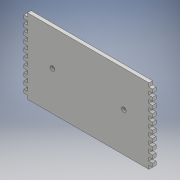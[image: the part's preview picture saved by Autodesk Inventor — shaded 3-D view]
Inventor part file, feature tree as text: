
AUTODESK INVENTOR PART (.ipt)
format: ipt  version: 2017 (Build 210142000, 142)  size: 253,952 bytes
history: native  units: mm
features: extrude x1, sketch x1
ambient origin geometry x8: Origin, YZ Plane, XZ Plane, XY Plane, X Axis, Y Axis, Z Axis, Center Point
bodies: Body1 (feature_tree)
feature tree (2):
  extrude  "Extrusion4"  Depth=6.35mm
  sketch  "Sketch5"  dims[d59=7.9375mm d73=6.35mm d79=6.35mm d80=6.35mm d81=6.35mm d82=6.35mm d92=6.35mm d93=6.35mm d94=6.35mm d95=6.35mm d96=6.35mm d97=6.35mm d100=6.35mm d101=6.35mm d102=6.35mm d103=6.35mm d106=6.35mm d107=6.35mm d108=6.35mm d109=6.35mm d112=6.35mm d113=6.35mm d114=6.35mm d115=6.35mm d118=6.35mm d119=6.35mm d120=6.35mm d121=6.35mm d124=6.35mm d125=6.35mm d126=6.35mm d127=6.35mm d130=6.35mm d131=6.35mm d132=6.35mm d133=6.35mm d136=6.35mm d137=6.35mm d138=6.35mm d139=6.35mm d143=6.35mm d149=6.35mm d150=6.35mm d151=6.35mm d152=6.35mm d153=6.35mm d154=6.35mm d155=6.35mm d156=6.35mm d157=6.35mm d158=6.35mm d159=6.35mm d160=6.35mm d161=6.35mm d162=6.35mm d163=6.35mm d164=6.35mm d165=6.35mm d166=6.35mm d167=6.35mm d168=6.35mm d169=6.35mm d170=6.35mm d171=6.35mm d172=6.35mm d173=6.35mm d174=6.35mm d175=6.35mm d176=6.35mm d177=6.35mm d178=6.35mm d179=6.35mm d180=6.35mm d181=6.35mm d182=6.35mm d183=6.35mm d184=6.35mm d185=6.35mm d186=6.35mm d187=6.35mm d188=6.35mm d189=6.35mm d190=6.35mm d192=50.8mm d193=50.8mm d194=215.9mm d195=63.5mm d196=63.5mm d197=6.35mm d198=0.0mm]
